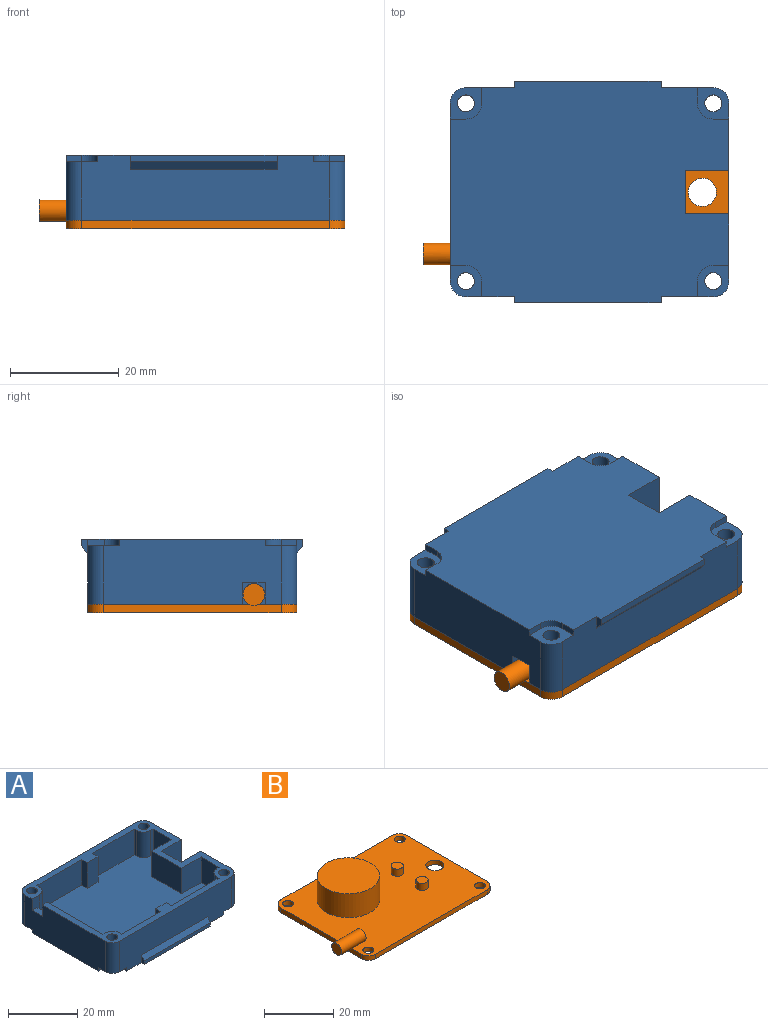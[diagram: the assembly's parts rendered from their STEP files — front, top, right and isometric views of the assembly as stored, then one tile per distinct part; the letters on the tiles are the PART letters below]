
ASSEMBLY  parts=2 mates=1
PART A: 73 faces, bbox 51.3x40.8x12 mm
  f0: plane 32.7x12mm, normal (-1,0,0), area 368.6mm2, adj f2,f5,f6,f7,f19,f53,f54,f55
  f1: plane 26.9x9mm, normal (1,0,0), area 225.3mm2, adj f2,f19,f45,f46,f71,f72
  f2: plane 51.3x38.5mm, normal (0,0,1), area 400mm2, adj f0,f1,f3,f4,f6,f7,f8,f9
  f3: plane 45.5x12mm, normal (0,1,0), area 468.8mm2, adj f2,f5,f6,f14,f57,f58,f59,f62
  f4: plane 45.5x12mm, normal (0,-1,0), area 467.2mm2, adj f2,f5,f7,f8,f49,f50,f51,f54
  f5: plane 51.3x40.81mm, normal (0,0,-1), area 1846.1mm2, adj f0,f3,f4,f9,f10,f11,f12,f13
  f6: cylinder r=2.9mm len=10.8mm, axis (0,0,-1), area 49.2mm2, adj f0,f2,f3,f58
  f7: cylinder r=2.9mm len=10.8mm, axis (0,0,-1), area 49.2mm2, adj f0,f2,f4,f54
  f8: cylinder r=2.9mm len=10.8mm, axis (0,0,-1), area 49.2mm2, adj f2,f4,f9,f50
  f9: plane 12.35x12mm, normal (1,0,0), area 144.7mm2, adj f2,f5,f8,f10,f47,f50
  f10: plane 12x8mm, normal (0,1,0), area 96mm2, adj f2,f5,f9,f11
  f11: plane 12x8mm, normal (1,0,0), area 96mm2, adj f2,f5,f10,f12
  f12: plane 12x8mm, normal (0,-1,0), area 96mm2, adj f2,f5,f11,f13
  f13: plane 12.35x12mm, normal (1,0,0), area 144.7mm2, adj f2,f5,f12,f14,f61,f62
  f14: cylinder r=2.9mm len=10.8mm, axis (0,0,-1), area 49.2mm2, adj f2,f3,f13,f62
  f15: cylinder r=1.55mm len=10.8mm, axis (0,0,-1), area 105.2mm2, adj f2,f50
  f16: cylinder r=1.55mm len=10.8mm, axis (0,0,-1), area 105.2mm2, adj f2,f58
  f17: cylinder r=1.55mm len=10.8mm, axis (0,0,-1), area 105.2mm2, adj f2,f62
  f18: cylinder r=1.55mm len=10.8mm, axis (0,0,-1), area 105.2mm2, adj f2,f54
  f19: plane 9x2.9mm, normal (0,-1,0), area 16.1mm2, adj f0,f1,f2,f20,f46,f72
  f20: cylinder r=2.9mm len=9mm, axis (0,0,-1), area 41mm2, adj f2,f19,f21,f46
  f21: plane 9x0.9mm, normal (1,0,0), area 8.1mm2, adj f2,f20,f22,f46
  f22: plane 18.23x9mm, normal (0,-1,0), area 164mm2, adj f2,f21,f23,f46
  f23: plane 9x2.29mm, normal (-1,0,0), area 20.6mm2, adj f2,f22,f24,f46
  f24: plane 9x4.38mm, normal (0,-1,0), area 39.4mm2, adj f2,f23,f25,f46
  f25: plane 9x2.29mm, normal (1,0,0), area 20.6mm2, adj f2,f24,f26,f46
  f26: plane 17.1x9mm, normal (0,-1,0), area 153.9mm2, adj f2,f25,f27,f46
  f27: plane 9x0.9mm, normal (-1,0,0), area 8.1mm2, adj f2,f26,f28,f46
  f28: cylinder r=2.9mm len=9mm, axis (0,0,-1), area 41mm2, adj f2,f27,f29,f46
  f29: plane 9x0.9mm, normal (0,-1,0), area 8.1mm2, adj f2,f28,f30,f46
  f30: plane 9x7.45mm, normal (-1,0,0), area 67mm2, adj f2,f29,f31,f46
  f31: plane 9x8mm, normal (0,1,0), area 72mm2, adj f2,f30,f32,f46
  f32: plane 12.17x9mm, normal (-1,0,0), area 109.5mm2, adj f2,f31,f33,f46
  f33: plane 9x8mm, normal (0,-1,0), area 72mm2, adj f2,f32,f34,f46
  f34: plane 9x7.29mm, normal (-1,0,0), area 65.6mm2, adj f2,f33,f35,f46
  f35: plane 9x0.9mm, normal (0,1,0), area 8.1mm2, adj f2,f34,f36,f46
  f36: cylinder r=2.9mm len=9mm, axis (0,0,-1), area 41mm2, adj f2,f35,f37,f46
  f37: plane 9x0.9mm, normal (-1,0,0), area 8.1mm2, adj f2,f36,f38,f46
  f38: plane 19.49x9mm, normal (0,1,0), area 175.4mm2, adj f2,f37,f39,f46
  f39: plane 9x2.05mm, normal (1,0,0), area 18.4mm2, adj f2,f38,f40,f46
  f40: plane 9x4.24mm, normal (0,1,0), area 38.2mm2, adj f2,f39,f41,f46
  f41: plane 9x2.05mm, normal (-1,0,0), area 18.4mm2, adj f2,f40,f42,f46
  f42: plane 15.98x9mm, normal (0,1,0), area 143.8mm2, adj f2,f41,f43,f46
  f43: plane 9x1.05mm, normal (1,0,0), area 9.5mm2, adj f2,f42,f44,f46
  f44: cylinder r=2.9mm len=9mm, axis (0,0,-1), area 39.6mm2, adj f2,f43,f45,f46
  f45: plane 9x0.9mm, normal (0,1,0), area 8.1mm2, adj f1,f2,f44,f46
  f46: plane 47.3x34.5mm, normal (0,0,1), area 1465.3mm2, adj f1,f19,f20,f21,f22,f23,f24,f25
  f47: plane 2.9x1.2mm, normal (0,-1,0), area 3.5mm2, adj f5,f9,f48,f50
  f48: cylinder r=2.9mm len=2.9mm, axis (0,0,-1), area 5.5mm2, adj f5,f47,f49,f50
  f49: plane 2.9x1.2mm, normal (1,0,0), area 3.5mm2, adj f4,f5,f48,f50
  f50: plane 5.8x5.8mm, normal (0,0,-1), area 22.5mm2, adj f4,f8,f9,f15,f47,f48,f49
  f51: plane 3.05x1.2mm, normal (-1,0,0), area 3.7mm2, adj f4,f5,f52,f54
  f52: cylinder r=2.9mm len=2.9mm, axis (0,0,-1), area 5.3mm2, adj f5,f51,f53,f54
  f53: plane 2.9x1.2mm, normal (0,-1,0), area 3.5mm2, adj f0,f5,f52,f54
  f54: plane 5.8x5.8mm, normal (0,0,-1), area 22.5mm2, adj f0,f4,f7,f18,f51,f52,f53
  f55: plane 2.9x1.2mm, normal (0,1,0), area 3.5mm2, adj f0,f5,f56,f58
  f56: cylinder r=2.9mm len=2.9mm, axis (0,0,-1), area 5.5mm2, adj f5,f55,f57,f58
  f57: plane 2.9x1.2mm, normal (-1,0,0), area 3.5mm2, adj f3,f5,f56,f58
  f58: plane 5.8x5.8mm, normal (0,0,-1), area 22.5mm2, adj f0,f3,f6,f16,f55,f56,f57
  f59: plane 2.9x1.2mm, normal (1,0,0), area 3.5mm2, adj f3,f5,f60,f62
  f60: cylinder r=2.9mm len=2.9mm, axis (0,0,-1), area 5.5mm2, adj f5,f59,f61,f62
  f61: plane 2.9x1.2mm, normal (0,1,0), area 3.5mm2, adj f5,f13,f60,f62
  f62: plane 5.8x5.8mm, normal (0,0,-1), area 22.5mm2, adj f3,f13,f14,f17,f59,f60,f61
  f63: plane 27x1.46mm, normal (0,-0.78,0.63), area 50.9mm2, adj f4,f64,f65,f66
  f64: plane 2.66x1.19mm, normal (-1,0,0), area 2.3mm2, adj f4,f5,f63,f66
  f65: plane 2.66x1.19mm, normal (1,0,0), area 2.3mm2, adj f4,f5,f63,f66
  f66: plane 27x1.2mm, normal (0,-1,0), area 32.4mm2, adj f5,f63,f64,f65
  f67: plane 27x1.2mm, normal (0,1,0), area 32.4mm2, adj f5,f68,f69,f70
  f68: plane 27x1.4mm, normal (0,0.78,0.62), area 48.4mm2, adj f3,f67,f69,f70
  f69: plane 2.6x1.12mm, normal (-1,0,0), area 2.1mm2, adj f3,f5,f67,f68
  f70: plane 2.6x1.12mm, normal (1,0,0), area 2.1mm2, adj f3,f5,f67,f68
  f71: plane 4x2mm, normal (0,1,0), area 8mm2, adj f0,f1,f2,f72
  f72: plane 4.2x2mm, normal (0,0,1), area 8.4mm2, adj f0,f1,f19,f71
PART B: 24 faces, bbox 56.3x38.5x10 mm
  f0: cylinder r=2mm len=10mm, axis (1,0,0), area 116.6mm2, adj f1,f2,f3,f16
  f1: plane 4x4mm, normal (-1,0,0), area 12.6mm2, adj f0
  f2: plane 4x3.8mm, normal (1,0,0), area 12.3mm2, adj f0,f16
  f3: plane 32.7x1.6mm, normal (-1,0,0), area 52.1mm2, adj f0,f4,f14,f16,f17
  f4: cylinder r=2.9mm len=2.9mm, axis (0,0,-1), area 7.3mm2, adj f3,f5,f16,f17
  f5: plane 45.5x1.6mm, normal (0,-1,0), area 72.8mm2, adj f4,f6,f16,f17
  f6: cylinder r=2.9mm len=2.9mm, axis (0,0,-1), area 7.3mm2, adj f5,f7,f16,f17
  f7: plane 32.7x1.6mm, normal (1,0,0), area 52.3mm2, adj f6,f8,f16,f17
  f8: cylinder r=2.9mm len=2.9mm, axis (0,0,-1), area 7.3mm2, adj f7,f9,f16,f17
  f9: plane 45.5x1.6mm, normal (0,1,0), area 72.8mm2, adj f8,f14,f16,f17
  f10: cylinder r=1.55mm len=3.1mm, axis (0,0,-1), area 15.6mm2, adj f16,f17
  f11: cylinder r=1.55mm len=3.1mm, axis (0,0,-1), area 15.6mm2, adj f16,f17
  f12: cylinder r=1.55mm len=3.1mm, axis (0,0,-1), area 15.6mm2, adj f16,f17
  f13: cylinder r=2.6mm len=5.2mm, axis (0,0,-1), area 26.1mm2, adj f16,f17
  f14: cylinder r=2.9mm len=2.9mm, axis (0,0,-1), area 7.3mm2, adj f3,f9,f16,f17
  f15: cylinder r=1.55mm len=3.1mm, axis (0,0,-1), area 15.6mm2, adj f16,f17
  f16: plane 51.3x38.5mm, normal (0,0,1), area 1634mm2, adj f0,f2,f3,f4,f5,f6,f7,f8
  f17: plane 51.3x38.5mm, normal (0,0,-1), area 1916.4mm2, adj f3,f4,f5,f6,f7,f8,f9,f10
  f18: cylinder r=9mm len=18mm, axis (0,0,-1), area 475mm2, adj f16,f19
  f19: plane 18x18mm, normal (0,0,1), area 254.5mm2, adj f18
  f20: cylinder r=1.75mm len=3.5mm, axis (0,0,-1), area 27.5mm2, adj f16,f21
  f21: plane 3.5x3.5mm, normal (0,0,1), area 9.6mm2, adj f20
  f22: cylinder r=1.75mm len=3.5mm, axis (0,0,-1), area 27.5mm2, adj f16,f23
  f23: plane 3.5x3.5mm, normal (0,0,1), area 9.6mm2, adj f22
PLACE A rot(axis=(1,0,0),180deg) t=(25.87,-42.44,26.06)mm
PLACE B t=(-5.93,-61.55,12.46)mm
MATE fastened B.f8 <-> A.f8  axis (0,0,1) through (42.47,-25.95,14.06)mm
